# Revit family: IS_CeraplusSafeOX_A7606_BIM_NL
name_source: partatom
category: Plumbing Fixtures
units: mm (PartAtom-declared; Revit-internal decimal feet)

## family parameters
Always vertical = No
Cut with Voids When Loaded = No
OmniClass Number = 23.31.11.00
Part Type = Normal
Room Calculation Point = No
Round Connector Dimension = Use Diameter
Shared = No
Work Plane-Based = No

## types (1)
- A7606AA - CERAPLUS SAFE OX SHR THM
    Accesoires = https://www.idealstandard.nl
    Afmetingen = 240 x 140 x 83 mm
    AfstandsEenheid = Millimeter
    Afwerking = Chrom
    Artikelnummer = A7606AA
    Artikelomschrijving = Ceraplus Safe OX, Thermostat-Brausemischer ohne Rückschlagventile, thermische Desinfektion, Kühlkörper, Ablage, Chrom
    Artikelreferentie = Ceraplus Safe OX, Thermostat-Brausemischer ohne Rückschlagventile, hohe Haltbarkeit, thermische Desinfektion, kühles Gehäuse, praktische Ablage mit ergonomischen Metallgriffen, Chrom
    Auteur = Ideal Standard
    BIMobject category = Taps & Mixers
    BIMobject category code = sanitary-taps-mixers
    BIMobject main category = Sanitary
    BIMobject main category code = sanitary
    Barcode = 4015413351980
    Beschrijvinggarantie = Herstellergarantie
    BimObjectNaam = _S_IdealStandard_Bathmixertaps_CeraplusSafeOX_A7606
    Brand url = https://www.idealstandard.nl
    Breedte = 240
    BrutoGewicht = 0
    Cost = 0 $
    Date of publishing = 18/05/2023
    Debiet = 10 l/min
    Default Elevation = 0 mm  [stored 0 ft]
    Description = Ceraplus Safe OX, Thermostatic Shower Mixer without Check Valves, Thermal Disinfection, Cool Body, Shelf, Chrome
    Diepte = 140 mm
    DuurEenheid = Bar
    Edition number = 1
    Eigenschappen = Ceraplus Safe OX, Thermostat-Brausemischer ohne Rückschlagventile, thermische Desinfektion, Kühlkörper, Ablage, Chrom
    GTIN code = https://4015413351980
    Garantieonderdelen = 5
    Garantieunits = Jaren
    Hoogte = 83,0551452636719
    Hulp = https://www.idealstandard.nl
    IFC Classification = Sanitary Terminal
    IfcExportAs = IfcValveType
    IfcExportType = MIXING
    Installatieinstructies = https://www.idealstandard.nl
    Installation instructions = https://www.idealstandard.nl
    Kleur = Chrom
    Lengte = 0 mm  [stored 0 ft]
    Manufacturer = Ideal Standard
    Manufacturer name = Ideal Standard
    Masterformat 2014 Code = 22 41 39
    Masterformat 2014 Description = Residential Faucets, Supplies, and Trim
    Materiaal = Messing
    Material main = Brass
    Model = A7606AA
    NBS Reference Code = 45-35-70/315
    NBS Reference Description = Taps and water supply fittings for baths
    Nettogewicht = 2.63
    NominalDepth = 140 mm
    NominalHeight = 83 mm
    NominalWidth = 240 mm
    OmniClass Code = 23-31 11 00
    OmniClass Description = Faucets
    Product Guid = 59a60487-1ae6-40cf-a8b0-d6f4b70cd04b
    Product SKU = A7606
    Product certification = https://www.idealstandard.nl
    Product data url = https://bimobject.com
    Product family = OX THM
    Product group = OX THM
    Product name = CERAPLUS SAFE OX SHR THM
    Product url = https://www.idealstandard.nl
    Productinformatie = https://www.idealstandard.nl
    QR code = http://bimobject.com
    Revisie = 1
    Size = 240 x 140 x 83 mm
    Technical description = https://www.idealstandard.nl
    Telefoonnummer = 077 355 08 08
    Testdruk = 10 bar
    UNSPSC Code = 301815
    URL = https://www.idealstandard.nl
    Uniclass 1.4 Code = L725111
    Uniclass 1.4 Description = Mixer taps
    Uniclass 2.0 Code = PR-35-06-82
    Uniclass 2.0 Description = Shower Mixers
    Uniclass 2015 Code = SL_35_80_80
    Uniclass 2015 Name = Showers
    Uniclass2015Beschrijving = Shower manual water supply sets
    Uniclass2015Referentie = Pr_40_20_87_78
    Uniclass2015Version = v1.22
    Urlproducent = https://www.idealstandard.nl
    ValutaEenheid = Euro
    Versie = 1
    Vervangingskosten = 0
    Volumeunits = Liter
    Vorm = Zylinder
    Wisselstukken = https://www.idealstandard.nl
    Youtube clip = https://www.youtube.com

note: [stored X ft] marks values corroborated as IEEE doubles in the binary element streams (Revit-internal decimal feet)

## geometry (parser evidence)
native form markers: Blend x4, Sweep x2
no freeform markers — native parametric forms only
